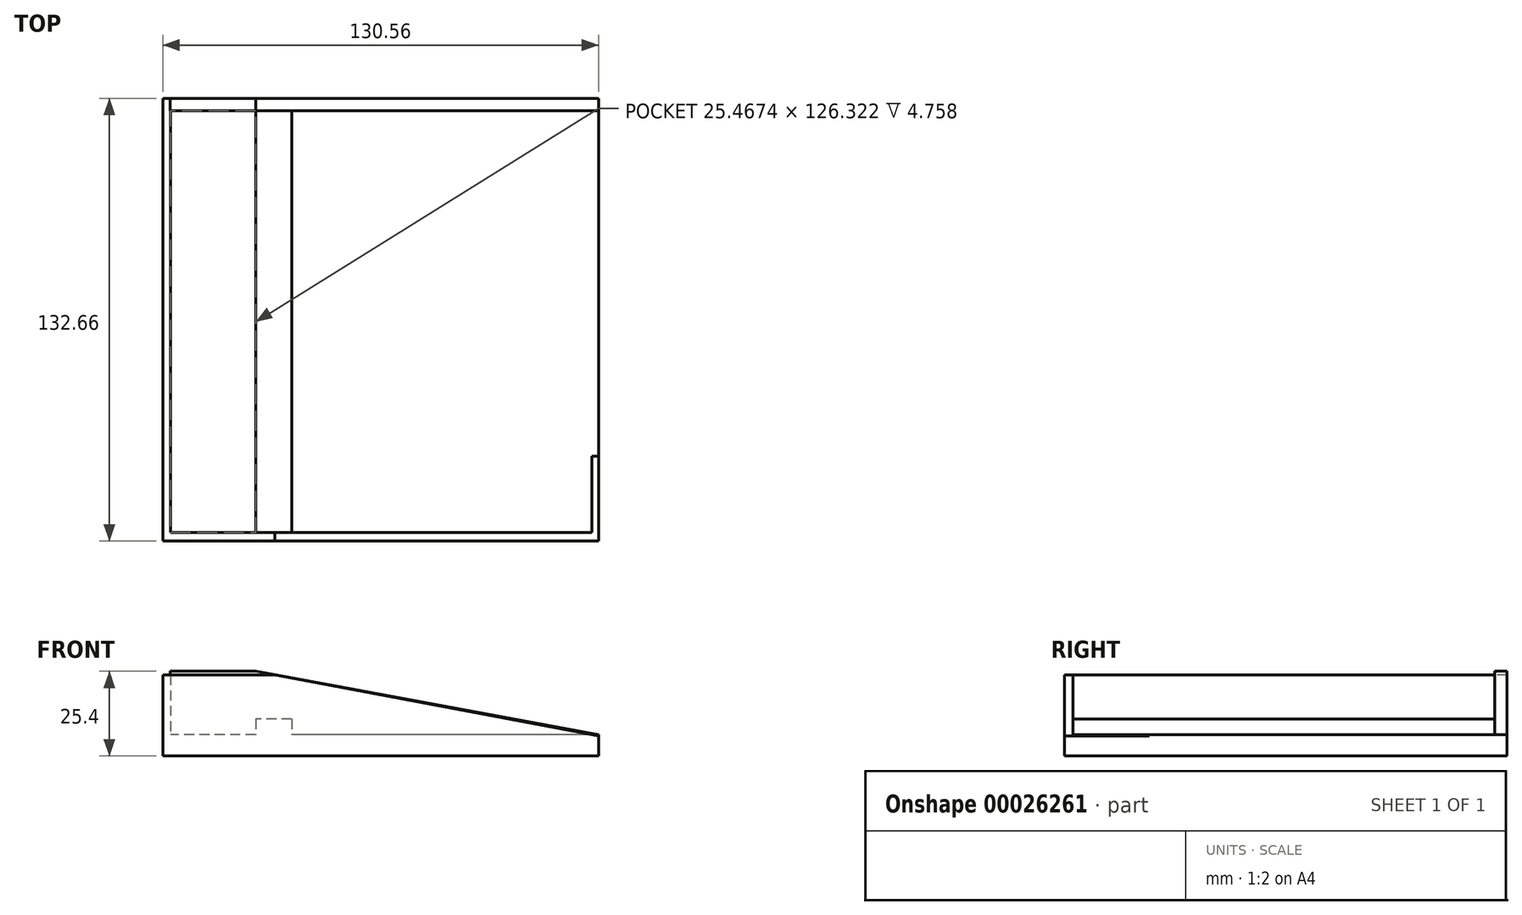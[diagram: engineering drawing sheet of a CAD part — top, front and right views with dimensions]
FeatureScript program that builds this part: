
annotation { "Feature Type Name" : "Feature", "Feature Type Description" : "" }
export const myFeature = defineFeature(function(context is Context, id is Id, definition is map)
    precondition{}
    {
        {
            var Q0;
            Q0=qCreatedBy(makeId("Top.planeOp"),FACE);
            var sketch = newSketch(context, id + "F0", { "sketchPlane" : qUnion([Q0])});
            skLineSegment(sketch, "E0.bottom", {"start": v(-70.94, 67.62) * mm, "end": v(59.62, 67.62) * mm});
            skLineSegment(sketch, "E0.top", {"start": v(-70.94, -65.04) * mm, "end": v(59.62, -65.04) * mm});
            skLineSegment(sketch, "E0.left", {"start": v(-70.94, 67.62) * mm, "end": v(-70.94, -65.04) * mm});
            skLineSegment(sketch, "E0.right", {"start": v(59.62, 67.62) * mm, "end": v(59.62, -65.04) * mm});
            skSolve(sketch);
        }
        {
            var Q0;
            Q0=makeQuery(id+"F0.imprint","IMPRINT",FACE,{"disambiguationData":[TD([[makeQuery(id+"F0.imprint","IMPRINT",EDGE,{"derivedFrom":sQuery(id+"F0.wireOp",EDGE,"E0.bottom")}),-1.0]])]});
            extrude(context, id + "F1", {"entities" : qUnion([Q0]), "depth" : 6.35 * mm});
        }
        {
            var Q0;
            Q0=makeQuery(id+"F1.opExtrude","CAP_FACE",FACE,{"disambiguationData":[OSD([sQuery(id+"F0.wireOp",EDGE,"E0.bottom"),sQuery(id+"F0.wireOp",EDGE,"E0.top"),sQuery(id+"F0.wireOp",EDGE,"E0.left"),sQuery(id+"F0.wireOp",EDGE,"E0.right")])],"isStart":false});
            var sketch = newSketch(context, id + "F2", { "sketchPlane" : qUnion([Q0])});
            skLineSegment(sketch, "E1", {"start": v(59.62, -62.47) * mm, "end": v(-70.94, -62.47) * mm});
            skLineSegment(sketch, "E2", {"start": v(-70.94, 49.13) * mm, "end": v(59.62, 49.13) * mm});
            skLineSegment(sketch, "E3", {"start": v(-68.6, 49.13) * mm, "end": v(-68.6, -62.47) * mm});
            skSolve(sketch);
        }
        {
            var Q0;
            {var subQ5=sQuery(id+"F2.wireOp",EDGE,"E3");Q0=makeQuery(id+"F2.imprint","IMPRINT",FACE,{"disambiguationData":[TD([[makeQuery(id+"F2.imprint","IMPRINT",EDGE,{"derivedFrom":subQ5}),-1.0]])]});}
            var Q1;
            {var subQ3=makeQuery(id+"F1.opExtrude","CAP_EDGE",EDGE,{"disambiguationData":[OSD([sQuery(id+"F0.wireOp",EDGE,"E0.top")])],"isStart":false});Q1=makeQuery(id+"F2.imprint","IMPRINT",FACE,{"disambiguationData":[TD([[makeQuery(id+"F2.imprint","IMPRINT",EDGE,{"derivedFrom":subQ3}),1.0]])]});}
            var Q2;
            {var subQ3=makeQuery(id+"F1.opExtrude","CAP_EDGE",EDGE,{"disambiguationData":[OSD([sQuery(id+"F0.wireOp",EDGE,"E0.bottom")])],"isStart":false});Q2=makeQuery(id+"F2.imprint","IMPRINT",FACE,{"disambiguationData":[TD([[makeQuery(id+"F2.imprint","IMPRINT",EDGE,{"derivedFrom":subQ3}),-1.0]])]});}
            extrude(context, id + "F3", {"entities" : qUnion([Q0, Q1, Q2]), "operationType" : NewBodyOperationType.ADD, "depth" : 17.92 * mm});
        }
        {
            var Q0;
            {var subQ0=sQuery(id+"F0.wireOp",EDGE,"E0.bottom");Q0=makeQuery(id+"F3.boolean.opBoolean","MERGE",FACE,{"derivedFrom":[makeQuery(id+"F1.opExtrude","SWEPT_FACE",FACE,{"disambiguationData":[OSD([subQ0])]}),makeQuery(id+"F3.opExtrude","SWEPT_FACE",FACE,{"disambiguationData":[OSD([subQ0])]})]});}
            var sketch = newSketch(context, id + "F4", { "sketchPlane" : qUnion([Q0])});
            skLineSegment(sketch, "E4.0", {"start": v(45.53, 25.4) * mm, "end": v(45.53, 0) * mm, "construction": true});
            skLineSegment(sketch, "E5", {"start": v(45.53, 25.4) * mm, "end": v(-59.62, 6.38) * mm});
            skLineSegment(sketch, "E6", {"start": v(-59.62, 6.38) * mm, "end": v(-62.01, 6.38) * mm});
            skSolve(sketch);
        }
        {
            var Q0;
            {var subQ0=sQuery(id+"F0.wireOp",EDGE,"E0.top");Q0=makeQuery(id+"F3.boolean.opBoolean","MERGE",FACE,{"derivedFrom":[makeQuery(id+"F1.opExtrude","SWEPT_FACE",FACE,{"disambiguationData":[OSD([subQ0])]}),makeQuery(id+"F3.opExtrude","SWEPT_FACE",FACE,{"disambiguationData":[OSD([subQ0])]})]});}
            var sketch = newSketch(context, id + "F5", { "sketchPlane" : qUnion([Q0])});
            skLineSegment(sketch, "E7", {"start": v(-37.03, 24.27) * mm, "end": v(59.62, 6.49) * mm});
            skSolve(sketch);
        }
        {
            var Q0;
            {var subQ3=sQuery(id+"F4.wireOp",EDGE,"E5");Q0=makeQuery(id+"F4.imprint","IMPRINT",FACE,{"disambiguationData":[TD([[makeQuery(id+"F4.imprint","IMPRINT",EDGE,{"derivedFrom":subQ3}),-1.0]])]});}
            var Q1;
            {var subQ3=sQuery(id+"F5.wireOp",EDGE,"E7");Q1=makeQuery(id+"F5.imprint","IMPRINT",FACE,{"disambiguationData":[TD([[makeQuery(id+"F5.imprint","IMPRINT",EDGE,{"derivedFrom":subQ3}),1.0]])]});}
            extrude(context, id + "F6", {"entities" : qUnion([Q0, Q1]), "operationType" : NewBodyOperationType.REMOVE, "oppositeDirection" : true, "depth" : 5.7 * mm});
        }
        {
            var Q0;
            {var subQ0=sQuery(id+"F0.wireOp",EDGE,"E0.top");Q0=makeQuery(id+"F3.boolean.opBoolean","MERGE",FACE,{"derivedFrom":[makeQuery(id+"F1.opExtrude","SWEPT_FACE",FACE,{"disambiguationData":[OSD([subQ0])]}),makeQuery(id+"F3.opExtrude","SWEPT_FACE",FACE,{"disambiguationData":[OSD([subQ0])]})]});}
            var sketch = newSketch(context, id + "F7", { "sketchPlane" : qUnion([Q0])});
            skLineSegment(sketch, "E8", {"start": v(-37.38, 0) * mm, "end": v(-37.38, 24.27) * mm});
            skLineSegment(sketch, "E9", {"start": v(-37.38, 24.27) * mm, "end": v(59.62, 5.97) * mm});
            skSolve(sketch);
        }
        {
            var Q0;
            {var subQ3=sQuery(id+"F7.wireOp",EDGE,"E9");Q0=makeQuery(id+"F7.imprint","IMPRINT",FACE,{"disambiguationData":[TD([[makeQuery(id+"F7.imprint","IMPRINT",EDGE,{"derivedFrom":subQ3}),1.0]])]});}
            extrude(context, id + "F8", {"entities" : qUnion([Q0]), "operationType" : NewBodyOperationType.REMOVE, "oppositeDirection" : true, "depth" : 25.4 * mm});
        }
        {
            var Q0;
            Q0=makeQuery(id+"F1.opExtrude","CAP_FACE",FACE,{"disambiguationData":[OSD([sQuery(id+"F0.wireOp",EDGE,"E0.bottom"),sQuery(id+"F0.wireOp",EDGE,"E0.top"),sQuery(id+"F0.wireOp",EDGE,"E0.left"),sQuery(id+"F0.wireOp",EDGE,"E0.right")])],"isStart":false});
            var sketch = newSketch(context, id + "F9", { "sketchPlane" : qUnion([Q0])});
            skLineSegment(sketch, "E10.bottom", {"start": v(-43.13, 49.13) * mm, "end": v(-32.27, 49.13) * mm});
            skLineSegment(sketch, "E10.top", {"start": v(-43.13, -62.47) * mm, "end": v(-32.27, -62.47) * mm});
            skLineSegment(sketch, "E10.left", {"start": v(-43.13, 49.13) * mm, "end": v(-43.13, -62.47) * mm});
            skLineSegment(sketch, "E10.right", {"start": v(-32.27, 49.13) * mm, "end": v(-32.27, -62.47) * mm});
            skSolve(sketch);
        }
        {
            var Q0;
            Q0 = qSketchRegion(id + "F9", true);
            extrude(context, id + "F10", {"entities" : qUnion([Q0]), "operationType" : NewBodyOperationType.ADD, "depth" : 4.76 * mm});
        }
        {
            var Q0;
            Q0=makeQuery(id+"F3.opExtrude","SWEPT_FACE",FACE,{"disambiguationData":[OSD([sQuery(id+"F2.wireOp",EDGE,"E2")])]});
            var sketch = newSketch(context, id + "F11", { "sketchPlane" : qUnion([Q0])});
            skLineSegment(sketch, "E11", {"start": v(-39.9, 24.27) * mm, "end": v(59.62, 6.35) * mm});
            skSolve(sketch);
        }
        {
            var Q0;
            {var subQ2=sQuery(id+"F11.wireOp",EDGE,"E11");Q0=makeQuery(id+"F11.imprint","IMPRINT",FACE,{"disambiguationData":[TD([[makeQuery(id+"F11.imprint","IMPRINT",EDGE,{"derivedFrom":subQ2}),1.0]])]});}
            extrude(context, id + "F12", {"entities" : qUnion([Q0]), "operationType" : NewBodyOperationType.REMOVE, "oppositeDirection" : true, "depth" : 25.4 * mm});
        }
        {
            var Q0;
            Q0=makeQuery(id+"F3.opExtrude","SWEPT_FACE",FACE,{"disambiguationData":[OSD([sQuery(id+"F2.wireOp",EDGE,"E2")])]});
            extrude(context, id + "F13", {"entities" : qUnion([Q0]), "operationType" : NewBodyOperationType.REMOVE, "oppositeDirection" : true, "depth" : 19.05 * mm});
        }
        {
            var Q0;
            {var subQ0=sQuery(id+"F0.wireOp",EDGE,"E0.bottom");var subQ1=sQuery(id+"F0.wireOp",EDGE,"E0.top");var subQ2=sQuery(id+"F0.wireOp",EDGE,"E0.right");var subQ3=makeQuery(id+"F1.opExtrude","CAP_FACE",FACE,{"disambiguationData":[OSD([subQ0,subQ1,sQuery(id+"F0.wireOp",EDGE,"E0.left"),subQ2])],"isStart":false});var subQ9=sQuery(id+"F2.wireOp",EDGE,"E2");var subQ12=makeQuery(id+"F1.opExtrude","SWEPT_FACE",FACE,{"disambiguationData":[OSD([subQ2])]});Q0=makeQuery(id+"F13.boolean.opBoolean","MERGE",FACE,{"derivedFrom":[makeQuery(id+"F10.boolean.opBoolean","SPLIT",FACE,{"disambiguationData":[TD([subQ12])],"derivedFrom":subQ3}),makeQuery(id+"F13.opExtrude","SWEPT_FACE",FACE,{"disambiguationData":[OSD([subQ9]),TDD([makeQuery(id+"F10.boolean.opBoolean","SPLIT",EDGE,{"disambiguationData":[TD([subQ12])],"derivedFrom":makeQuery(id+"F3.opExtrude","CAP_EDGE",EDGE,{"disambiguationData":[OSD([subQ9])],"isStart":true})})])]})]});}
            var sketch = newSketch(context, id + "F14", { "sketchPlane" : qUnion([Q0])});
            skPoint(sketch, "E12.oppositeSnap0", {"position": v(13.67, 67.62) * mm});
            skLineSegment(sketch, "E12.bottom", {"start": v(59.62, 63.86) * mm, "end": v(-68.76, 63.86) * mm});
            skLineSegment(sketch, "E12.top", {"start": v(59.62, 67.62) * mm, "end": v(-68.76, 67.62) * mm});
            skLineSegment(sketch, "E12.left", {"start": v(59.62, 63.86) * mm, "end": v(59.62, 67.62) * mm});
            skLineSegment(sketch, "E12.right", {"start": v(-68.76, 63.86) * mm, "end": v(-68.76, 67.62) * mm});
            skSolve(sketch);
        }
        {
            var Q0;
            {var subQ0=sQuery(id+"F14.wireOp",EDGE,"E12.left");Q0=makeQuery(id+"F14.imprint","IMPRINT",FACE,{"disambiguationData":[TD([[makeQuery(id+"F14.imprint","IMPRINT",EDGE,{"derivedFrom":subQ0}),-1.0]])]});}
            var Q1;
            {var subQ8=sQuery(id+"F14.wireOp",EDGE,"E12.right");Q1=makeQuery(id+"F14.imprint","IMPRINT",FACE,{"disambiguationData":[TD([[makeQuery(id+"F14.imprint","IMPRINT",EDGE,{"derivedFrom":subQ8}),-1.0]])]});}
            extrude(context, id + "F15", {"entities" : qUnion([Q0, Q1]), "operationType" : NewBodyOperationType.ADD, "depth" : 19.05 * mm});
        }
        {
            var Q0;
            Q0=makeQuery(id+"F15.opExtrude","SWEPT_FACE",FACE,{"disambiguationData":[OSD([sQuery(id+"F14.wireOp",EDGE,"E12.bottom")])]});
            var sketch = newSketch(context, id + "F16", { "sketchPlane" : qUnion([Q0])});
            skLineSegment(sketch, "E13", {"start": v(-43.13, 25.4) * mm, "end": v(59.62, 6.35) * mm});
            skSolve(sketch);
        }
        {
            var Q0;
            {var subQ2=sQuery(id+"F16.wireOp",EDGE,"E13");Q0=makeQuery(id+"F16.imprint","IMPRINT",FACE,{"disambiguationData":[TD([[makeQuery(id+"F16.imprint","IMPRINT",EDGE,{"derivedFrom":subQ2}),1.0]])]});}
            extrude(context, id + "F17", {"entities" : qUnion([Q0]), "operationType" : NewBodyOperationType.REMOVE, "oppositeDirection" : true, "depth" : 25.4 * mm});
        }
    });
